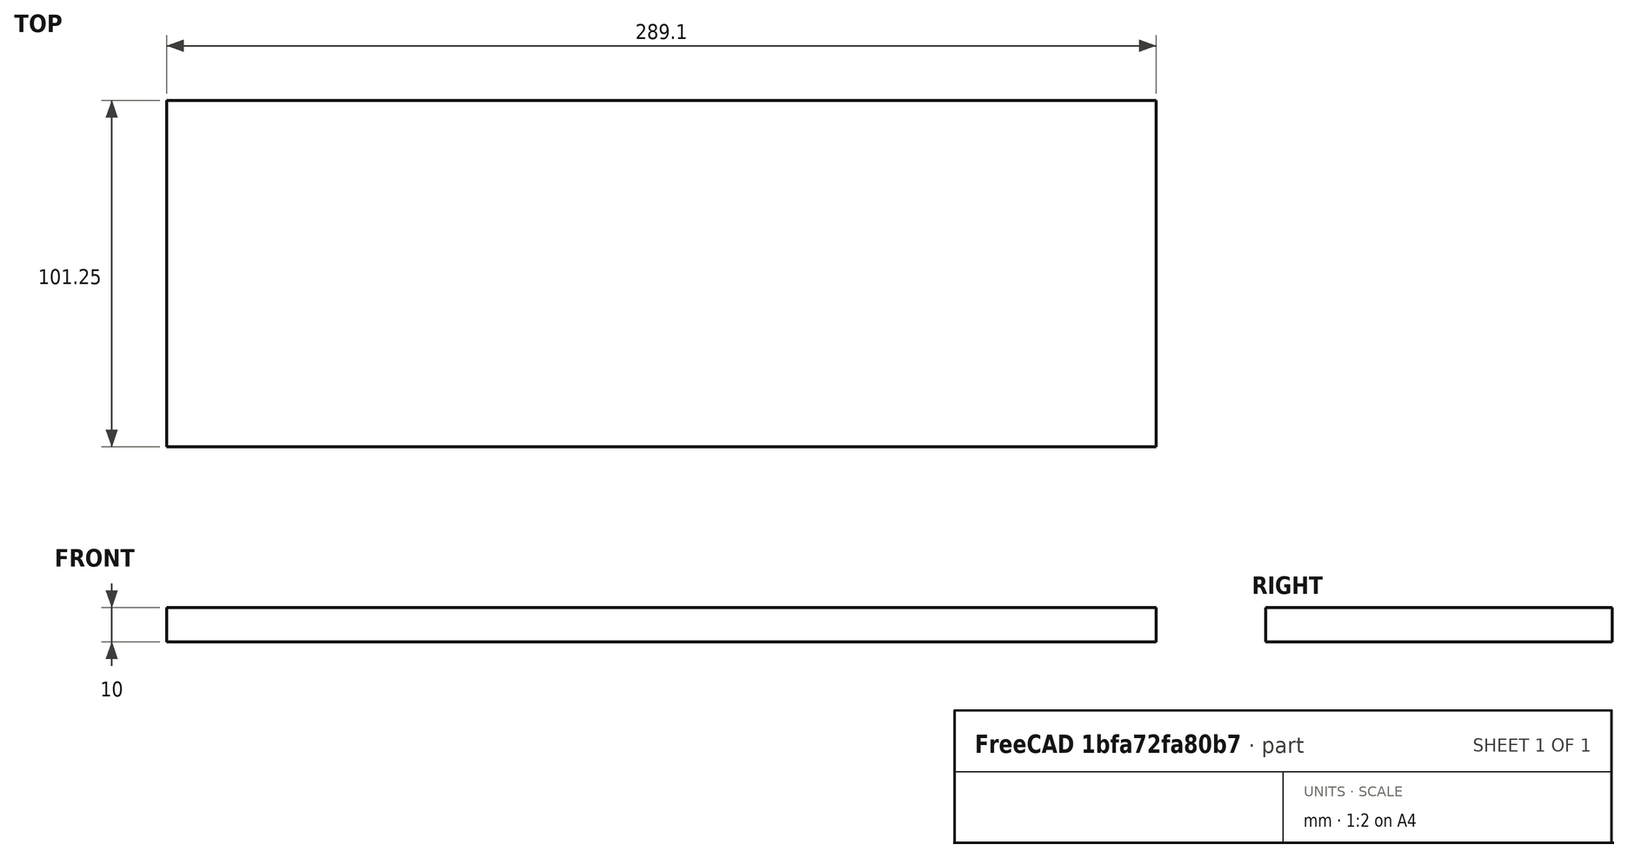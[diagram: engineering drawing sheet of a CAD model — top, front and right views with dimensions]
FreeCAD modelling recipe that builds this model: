
FCSTD DOCUMENT  (FreeCAD 0.21R33771 (Git))
Label: YawBearing_Extended_Side
License: All rights reserved
LicenseURL: http://en.wikipedia.org/wiki/All_rights_reserved
objects: Sketcher::SketchObject×1, PartDesign::Pad×1, PartDesign::Body×1, Spreadsheet::Sheet×1
note: 4 computed .brp shape members not serialized (recipe doc carries the construction recipe); baked Part::Feature solids carry a one-line shape summary decoded from their .brp
EXTERNAL_REF file=../../Master_of_Puppets.FCStd obj=Spreadsheet
EXTERNAL_REF file=../../Master_of_Puppets.FCStd obj=YawBearing

FEATURE [Sketcher::SketchObject] Sketch
  FullyConstrained = true
  MapMode = 5
  Support = -> [XY_Plane]
  expr: Constraints[10] = Spreadsheet.Width / 2
  expr: Constraints[11] = Spreadsheet.X
  expr: Constraints[8] = Spreadsheet.Width
  expr: Constraints[9] = Spreadsheet.SideLength
  sketch-geometry (4):
    g0: LineSegment StartX=-144.55 StartY=-50.625 StartZ=0 EndX=144.55 EndY=-50.625 EndZ=0
    g1: LineSegment StartX=144.55 StartY=-50.625 StartZ=0 EndX=144.55 EndY=50.625 EndZ=0
    g2: LineSegment StartX=144.55 StartY=50.625 StartZ=0 EndX=-144.55 EndY=50.625 EndZ=0
    g3: LineSegment StartX=-144.55 StartY=50.625 StartZ=0 EndX=-144.55 EndY=-50.625 EndZ=0
  constraints (12):
    c: Coincident(g0,g1)
    c: Coincident(g1,g2)
    c: Coincident(g2,g3)
    c: Coincident(g3,g0)
    c: Horizontal(g0)
    c: Horizontal(g2)
    c: Vertical(g1)
    c: Vertical(g3)
    c: DistanceY(g1,g1) = 101.25
    c: DistanceX(g2,g2) = 289.1
    c: DistanceY(g-1,g2) = 50.625
    c: Distance(g-1,g1) = 144.55
FEATURE [PartDesign::Pad] Pad
  AllowMultiFace = false
  Direction = (0,0,1)
  Length = 10
  Length2 = 100
  Profile = -> Sketch
  Type = 0
  expr: Length = Spreadsheet.FlatMetalThickness
FEATURE [PartDesign::Body] Body  label="YawBearing_Extended_Side"
  Group = -> [Sketch,Pad]
  Openafpm_Flat = true
  Origin = -> Origin
  Placement = pos=(144.55,50.625,0) rot=(0,0,1;0rad)
  Tip = -> Pad
  expr: .Placement.Base.x = Spreadsheet.X
  expr: .Placement.Base.y = Spreadsheet.Y
  expr: .Placement.Base.z = Spreadsheet.Z
FEATURE [Spreadsheet::Sheet] Spreadsheet
  cells = A1='Inputs; A2='FlatMetalThickness; B2(FlatMetalThickness)==Master_of_Puppets#Spreadsheet.FlatMetalThickness; A3='Width; B3(Width)==Master_of_Puppets#YawBearing.SideWidth; A4='SideLength; B4(SideLength)==Master_of_Puppets#YawBearing.SideLength; A5='Placement; A6='X; B6='Y; C6='Z; A7(X)==SideLength / 2; B7(Y)==Width / 2; C7(Z)=0
